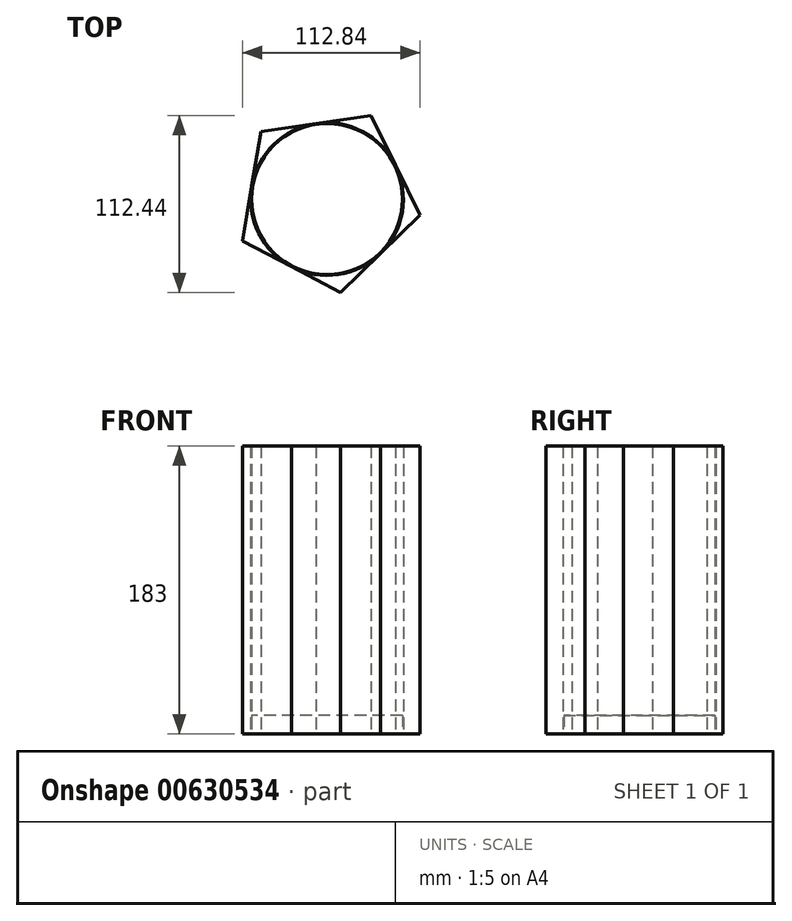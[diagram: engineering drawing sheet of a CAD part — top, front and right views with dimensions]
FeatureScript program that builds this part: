
annotation { "Feature Type Name" : "Feature", "Feature Type Description" : "" }
export const myFeature = defineFeature(function(context is Context, id is Id, definition is map)
    precondition{}
    {
        {
            var Q0;
            Q0=qCreatedBy(makeId("Top.planeOp"),FACE);
            var sketch = newSketch(context, id + "F0", { "sketchPlane" : qUnion([Q0])});
            skCircle(sketch, "E0.cCircle", {"center": v(3.37, 0) * mm, "radius": 48.5 * mm, "construction": true});
            skLineSegment(sketch, "E0.0", {"start": v(31.18, 53.12) * mm, "end": v(62.48, -10.04) * mm});
            skLineSegment(sketch, "E0.1", {"start": v(62.48, -10.04) * mm, "end": v(12.08, -59.32) * mm});
            skLineSegment(sketch, "E0.2", {"start": v(12.08, -59.32) * mm, "end": v(-50.36, -26.62) * mm});
            skLineSegment(sketch, "E0.3", {"start": v(-50.36, -26.62) * mm, "end": v(-38.56, 42.87) * mm});
            skLineSegment(sketch, "E0.4", {"start": v(-38.56, 42.87) * mm, "end": v(31.18, 53.12) * mm});
            skPoint(sketch, "E0.0.midPoint", {"position": v(46.83, 21.54) * mm});
            skSolve(sketch);
        }
        {
            var Q0;
            Q0 = qSketchRegion(id + "F0", true);
            extrude(context, id + "F1", {"entities" : qUnion([Q0]), "depth" : 80 * mm, "offsetDistance" : 25 * mm});
        }
        {
            var Q0;
            Q0=makeQuery(id+"F0.imprint","IMPRINT",FACE,{"disambiguationData":[TD([[makeQuery(id+"F0.imprint","IMPRINT",EDGE,{"derivedFrom":sQuery(id+"F0.wireOp",EDGE,"E0.0")}),-1.0]])]});
            var sketch = newSketch(context, id + "F2", { "sketchPlane" : qUnion([Q0])});
            skLineSegment(sketch, "E1.0.0", {"start": v(31.18, 53.12) * mm, "end": v(-38.56, 42.87) * mm});
            skLineSegment(sketch, "E1.0.1", {"start": v(-38.56, 42.87) * mm, "end": v(-50.36, -26.62) * mm});
            skLineSegment(sketch, "E1.0.2", {"start": v(-50.36, -26.62) * mm, "end": v(12.08, -59.32) * mm});
            skLineSegment(sketch, "E1.0.3", {"start": v(12.08, -59.32) * mm, "end": v(62.48, -10.04) * mm});
            skLineSegment(sketch, "E1.0.4", {"start": v(62.48, -10.04) * mm, "end": v(31.18, 53.12) * mm});
            skCircle(sketch, "E2.0", {"center": v(3.37, 0) * mm, "radius": 48.5 * mm});
            skSolve(sketch);
        }
        {
            var Q0;
            {var subQ0=sQuery(id+"F2.wireOp",EDGE,"E1.0.4");var subQ1=sQuery(id+"F2.wireOp",EDGE,"E1.0.0");var subQ2=makeQuery(id+"F2.imprint","INTERSECT",VERTEX,{"derivedFrom":[subQ1,subQ0]});Q0=makeQuery(id+"F2.imprint","IMPRINT",FACE,{"disambiguationData":[TD([[makeQuery(id+"F2.imprint","IMPRINT",EDGE,{"disambiguationData":[TD([[subQ2,1.0]])],"derivedFrom":subQ1}),-1.0]])]});}
            var Q1;
            {var subQ0=sQuery(id+"F2.wireOp",EDGE,"E1.0.1");var subQ1=sQuery(id+"F2.wireOp",EDGE,"E1.0.0");var subQ2=makeQuery(id+"F2.imprint","INTERSECT",VERTEX,{"derivedFrom":[subQ1,subQ0]});Q1=makeQuery(id+"F2.imprint","IMPRINT",FACE,{"disambiguationData":[TD([[makeQuery(id+"F2.imprint","IMPRINT",EDGE,{"disambiguationData":[TD([[subQ2,-1.0]])],"derivedFrom":subQ1}),-1.0]])]});}
            var Q2;
            {var subQ0=sQuery(id+"F2.wireOp",EDGE,"E1.0.2");var subQ1=sQuery(id+"F2.wireOp",EDGE,"E1.0.1");var subQ2=makeQuery(id+"F2.imprint","INTERSECT",VERTEX,{"derivedFrom":[subQ1,subQ0]});Q2=makeQuery(id+"F2.imprint","IMPRINT",FACE,{"disambiguationData":[TD([[makeQuery(id+"F2.imprint","IMPRINT",EDGE,{"disambiguationData":[TD([[subQ2,-1.0]])],"derivedFrom":subQ1}),-1.0]])]});}
            var Q3;
            {var subQ0=sQuery(id+"F2.wireOp",EDGE,"E1.0.3");var subQ1=sQuery(id+"F2.wireOp",EDGE,"E1.0.2");var subQ2=makeQuery(id+"F2.imprint","INTERSECT",VERTEX,{"derivedFrom":[subQ1,subQ0]});Q3=makeQuery(id+"F2.imprint","IMPRINT",FACE,{"disambiguationData":[TD([[makeQuery(id+"F2.imprint","IMPRINT",EDGE,{"disambiguationData":[TD([[subQ2,-1.0]])],"derivedFrom":subQ1}),-1.0]])]});}
            var Q4;
            {var subQ0=sQuery(id+"F2.wireOp",EDGE,"E1.0.4");var subQ1=sQuery(id+"F2.wireOp",EDGE,"E1.0.3");var subQ2=makeQuery(id+"F2.imprint","INTERSECT",VERTEX,{"derivedFrom":[subQ1,subQ0]});Q4=makeQuery(id+"F2.imprint","IMPRINT",FACE,{"disambiguationData":[TD([[makeQuery(id+"F2.imprint","IMPRINT",EDGE,{"disambiguationData":[TD([[subQ2,-1.0]])],"derivedFrom":subQ1}),-1.0]])]});}
            extrude(context, id + "F3", {"entities" : qUnion([Q0, Q1, Q2, Q3, Q4]), "operationType" : NewBodyOperationType.REMOVE, "depth" : 285 * mm, "offsetDistance" : 25 * mm});
        }
        {
            var Q0;
            Q0=makeQuery(id+"F1.opExtrude","CAP_FACE",FACE,{"disambiguationData":[OSD([sQuery(id+"F0.wireOp",EDGE,"E0.0"),sQuery(id+"F0.wireOp",EDGE,"E0.1"),sQuery(id+"F0.wireOp",EDGE,"E0.2"),sQuery(id+"F0.wireOp",EDGE,"E0.3"),sQuery(id+"F0.wireOp",EDGE,"E0.4")])],"isStart":false});
            extrude(context, id + "F4", {"entities" : qUnion([Q0]), "operationType" : NewBodyOperationType.REMOVE, "oppositeDirection" : true, "depth" : 80 * mm, "offsetDistance" : 25 * mm});
        }
        {
            var Q0;
            Q0=makeQuery(id+"F0.imprint","IMPRINT",FACE,{"disambiguationData":[TD([[makeQuery(id+"F0.imprint","IMPRINT",EDGE,{"derivedFrom":sQuery(id+"F0.wireOp",EDGE,"E0.0")}),-1.0]])]});
            var sketch = newSketch(context, id + "F5", { "sketchPlane" : qUnion([Q0])});
            skLineSegment(sketch, "E3.0.0", {"start": v(31.18, 53.12) * mm, "end": v(-38.56, 42.87) * mm});
            skLineSegment(sketch, "E3.0.1", {"start": v(-38.56, 42.87) * mm, "end": v(-50.36, -26.62) * mm});
            skLineSegment(sketch, "E3.0.2", {"start": v(-50.36, -26.62) * mm, "end": v(12.08, -59.32) * mm});
            skLineSegment(sketch, "E3.0.3", {"start": v(12.08, -59.32) * mm, "end": v(62.48, -10.04) * mm});
            skLineSegment(sketch, "E3.0.4", {"start": v(62.48, -10.04) * mm, "end": v(31.18, 53.12) * mm});
            skCircle(sketch, "E4.0", {"center": v(3.37, 0) * mm, "radius": 48.5 * mm});
            skSolve(sketch);
        }
        {
            var Q0;
            {var subQ0=sQuery(id+"F5.wireOp",EDGE,"E3.0.3");var subQ1=sQuery(id+"F5.wireOp",EDGE,"E3.0.2");var subQ2=makeQuery(id+"F5.imprint","INTERSECT",VERTEX,{"derivedFrom":[subQ1,subQ0]});Q0=makeQuery(id+"F5.imprint","IMPRINT",FACE,{"disambiguationData":[TD([[makeQuery(id+"F5.imprint","IMPRINT",EDGE,{"disambiguationData":[TD([[subQ2,-1.0]])],"derivedFrom":subQ1}),-1.0]])]});}
            var Q1;
            {var subQ0=sQuery(id+"F5.wireOp",EDGE,"E3.0.2");var subQ1=sQuery(id+"F5.wireOp",EDGE,"E3.0.1");var subQ2=makeQuery(id+"F5.imprint","INTERSECT",VERTEX,{"derivedFrom":[subQ1,subQ0]});Q1=makeQuery(id+"F5.imprint","IMPRINT",FACE,{"disambiguationData":[TD([[makeQuery(id+"F5.imprint","IMPRINT",EDGE,{"disambiguationData":[TD([[subQ2,-1.0]])],"derivedFrom":subQ1}),-1.0]])]});}
            var Q2;
            {var subQ0=sQuery(id+"F5.wireOp",EDGE,"E3.0.1");var subQ1=sQuery(id+"F5.wireOp",EDGE,"E3.0.0");var subQ2=makeQuery(id+"F5.imprint","INTERSECT",VERTEX,{"derivedFrom":[subQ1,subQ0]});Q2=makeQuery(id+"F5.imprint","IMPRINT",FACE,{"disambiguationData":[TD([[makeQuery(id+"F5.imprint","IMPRINT",EDGE,{"disambiguationData":[TD([[subQ2,-1.0]])],"derivedFrom":subQ1}),-1.0]])]});}
            var Q3;
            {var subQ0=sQuery(id+"F5.wireOp",EDGE,"E3.0.4");var subQ1=sQuery(id+"F5.wireOp",EDGE,"E3.0.0");var subQ2=makeQuery(id+"F5.imprint","INTERSECT",VERTEX,{"derivedFrom":[subQ1,subQ0]});Q3=makeQuery(id+"F5.imprint","IMPRINT",FACE,{"disambiguationData":[TD([[makeQuery(id+"F5.imprint","IMPRINT",EDGE,{"disambiguationData":[TD([[subQ2,1.0]])],"derivedFrom":subQ1}),-1.0]])]});}
            var Q4;
            {var subQ0=sQuery(id+"F5.wireOp",EDGE,"E3.0.4");var subQ1=sQuery(id+"F5.wireOp",EDGE,"E3.0.3");var subQ2=makeQuery(id+"F5.imprint","INTERSECT",VERTEX,{"derivedFrom":[subQ1,subQ0]});Q4=makeQuery(id+"F5.imprint","IMPRINT",FACE,{"disambiguationData":[TD([[makeQuery(id+"F5.imprint","IMPRINT",EDGE,{"disambiguationData":[TD([[subQ2,-1.0]])],"derivedFrom":subQ1}),-1.0]])]});}
            extrude(context, id + "F6", {"entities" : qUnion([Q0, Q1, Q2, Q3, Q4]), "depth" : 183 * mm, "offsetDistance" : 25 * mm});
        }
        {
            var Q0;
            Q0=makeQuery(id+"F0.imprint","IMPRINT",FACE,{"disambiguationData":[TD([[makeQuery(id+"F0.imprint","IMPRINT",EDGE,{"derivedFrom":sQuery(id+"F0.wireOp",EDGE,"E0.0")}),-1.0]])]});
            var sketch = newSketch(context, id + "F7", { "sketchPlane" : qUnion([Q0])});
            skPoint(sketch, "E5.0", {"position": v(3.37, 0) * mm});
            skCircle(sketch, "E6", {"center": v(3.37, 0) * mm, "radius": 48 * mm});
            skSolve(sketch);
        }
        {
            var Q0;
            Q0 = qSketchRegion(id + "F7", true);
            extrude(context, id + "F8", {"entities" : qUnion([Q0]), "depth" : 12 * mm, "offsetDistance" : 25 * mm});
        }
    });
